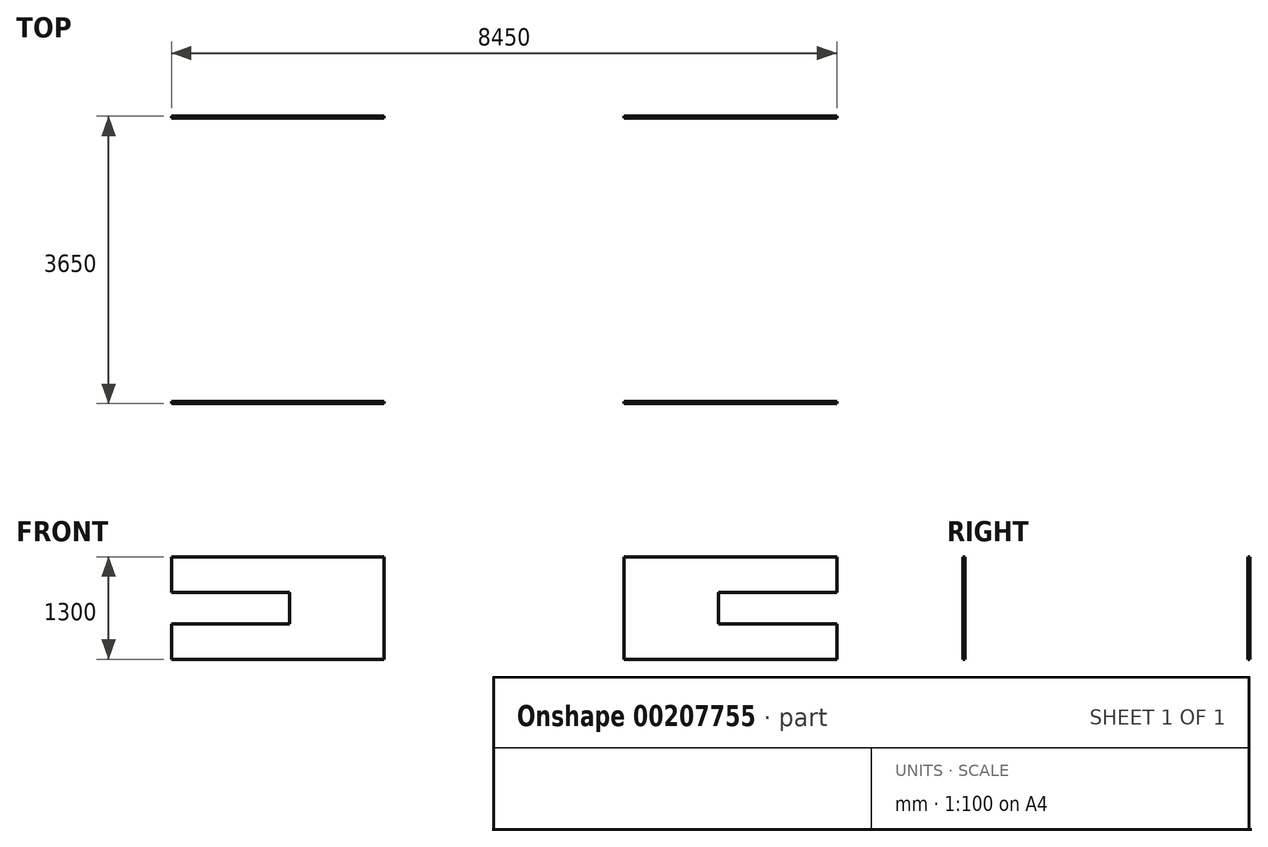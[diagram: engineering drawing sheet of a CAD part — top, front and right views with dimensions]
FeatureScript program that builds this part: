
annotation { "Feature Type Name" : "Feature", "Feature Type Description" : "" }
export const myFeature = defineFeature(function(context is Context, id is Id, definition is map)
    precondition{}
    {
        {
            var Q0;
            Q0=qCreatedBy(makeId("Front.planeOp"),FACE);
            cPlane(context, id + "F0", {"entities" : qUnion([Q0]), "cplaneType" : CPlaneType.OFFSET, "offset" : 1800 * mm, "width" : 150 * mm, "height" : 150 * mm});
        }
        {
            var Q0;
            Q0=qCreatedBy(id+"F0.planeOp",FACE);
            var sketch = newSketch(context, id + "F1", { "sketchPlane" : qUnion([Q0])});
            skLineSegment(sketch, "E0", {"start": v(1525, 1605) * mm, "end": v(1525, 305) * mm});
            skLineSegment(sketch, "E1", {"start": v(1525, 305) * mm, "end": v(4225, 305) * mm});
            skLineSegment(sketch, "E2", {"start": v(4225, 305) * mm, "end": v(4225, 755) * mm});
            skLineSegment(sketch, "E3", {"start": v(4225, 755) * mm, "end": v(2725, 755) * mm});
            skLineSegment(sketch, "E4", {"start": v(2725, 755) * mm, "end": v(2725, 1155) * mm});
            skLineSegment(sketch, "E5", {"start": v(2725, 1155) * mm, "end": v(4225, 1155) * mm});
            skLineSegment(sketch, "E6", {"start": v(4225, 1155) * mm, "end": v(4225, 1605) * mm});
            skLineSegment(sketch, "E7", {"start": v(4225, 1605) * mm, "end": v(1525, 1605) * mm});
            skSolve(sketch);
        }
        {
            var Q0;
            Q0=makeQuery(id+"F1.imprint","IMPRINT",FACE,{"disambiguationData":[TD([[makeQuery(id+"F1.imprint","IMPRINT",EDGE,{"derivedFrom":sQuery(id+"F1.wireOp",EDGE,"E0")}),1.0]])]});
            extrude(context, id + "F2", {"entities" : qUnion([Q0]), "depth" : 25 * mm, "offsetDistance" : 25 * mm});
        }
        {
            var Q0;
            Q0=makeQuery(id+"F2.opExtrude","SWEPT_BODY",BODY,{"disambiguationData":[OSD([sQuery(id+"F1.wireOp",EDGE,"E0"),sQuery(id+"F1.wireOp",EDGE,"E1"),sQuery(id+"F1.wireOp",EDGE,"E2"),sQuery(id+"F1.wireOp",EDGE,"E3"),sQuery(id+"F1.wireOp",EDGE,"E4"),sQuery(id+"F1.wireOp",EDGE,"E5"),sQuery(id+"F1.wireOp",EDGE,"E6"),sQuery(id+"F1.wireOp",EDGE,"E7")])]});
            var Q1;
            Q1=qCreatedBy(makeId("Right.planeOp"),FACE);
            mirror(context, id + "F3", {"entities" : qUnion([Q0]), "mirrorPlane" : qUnion([Q1])});
        }
        {
            var Q0;
            Q0=makeQuery(id+"F2.opExtrude","SWEPT_BODY",BODY,{"disambiguationData":[OSD([sQuery(id+"F1.wireOp",EDGE,"E0"),sQuery(id+"F1.wireOp",EDGE,"E1"),sQuery(id+"F1.wireOp",EDGE,"E2"),sQuery(id+"F1.wireOp",EDGE,"E3"),sQuery(id+"F1.wireOp",EDGE,"E4"),sQuery(id+"F1.wireOp",EDGE,"E5"),sQuery(id+"F1.wireOp",EDGE,"E6"),sQuery(id+"F1.wireOp",EDGE,"E7")])]});
            var Q1;
            Q1=makeQuery(id+"F3.opPattern","COPY",BODY,{"derivedFrom":makeQuery(id+"F2.opExtrude","SWEPT_BODY",BODY,{"disambiguationData":[OSD([sQuery(id+"F1.wireOp",EDGE,"E0"),sQuery(id+"F1.wireOp",EDGE,"E1"),sQuery(id+"F1.wireOp",EDGE,"E2"),sQuery(id+"F1.wireOp",EDGE,"E3"),sQuery(id+"F1.wireOp",EDGE,"E4"),sQuery(id+"F1.wireOp",EDGE,"E5"),sQuery(id+"F1.wireOp",EDGE,"E6"),sQuery(id+"F1.wireOp",EDGE,"E7")])]}),"instanceName":"1"});
            var Q2;
            Q2=qCreatedBy(makeId("Front.planeOp"),FACE);
            mirror(context, id + "F4", {"entities" : qUnion([Q0, Q1]), "mirrorPlane" : qUnion([Q2])});
        }
    });
